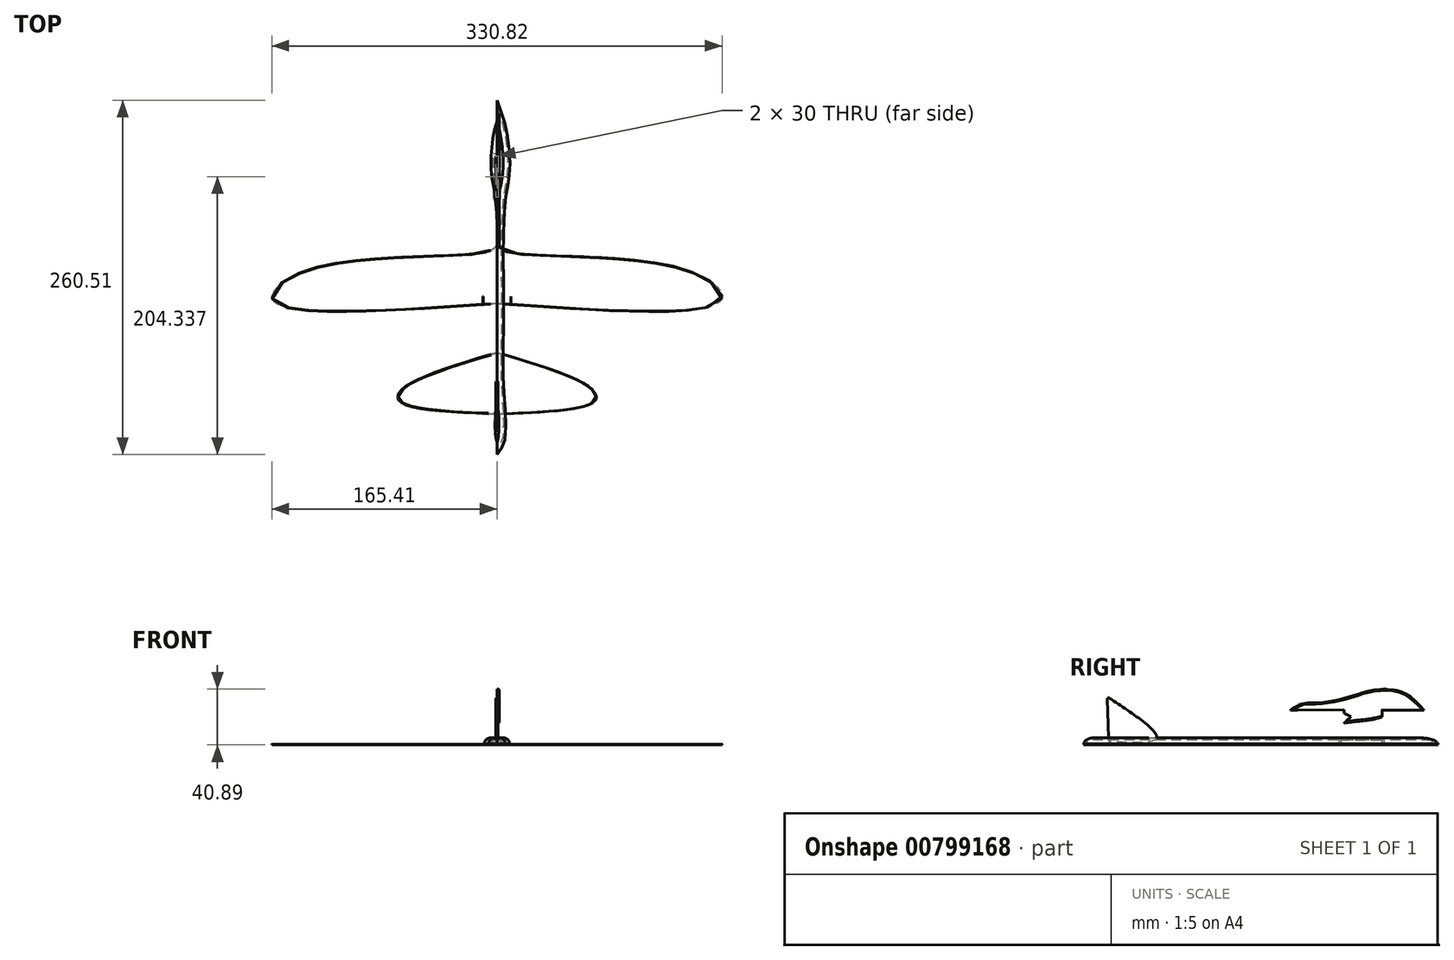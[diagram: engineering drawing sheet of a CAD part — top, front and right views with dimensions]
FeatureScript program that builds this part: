
annotation { "Feature Type Name" : "Feature", "Feature Type Description" : "" }
export const myFeature = defineFeature(function(context is Context, id is Id, definition is map)
    precondition{}
    {
        {
            var Q0;
            Q0=qCreatedBy(makeId("Top.planeOp"),FACE);
            var sketch = newSketch(context, id + "F0", { "sketchPlane" : qUnion([Q0])});
            skFitSpline(sketch, "E0", {"points": [v(0, 20.4) * mm, v(-6.56, 14.7) * mm, v(-134.74, 2.33) * mm, v(-164.69, -21.18) * mm, v(0, -23.65) * mm], "startDerivative": vector(-33.5, -72.01) * mm, "endDerivative": vector(609.3, 42.8) * mm});
            skFitSpline(sketch, "E1.MirrorCS", {"points": [v(0, 20.4) * mm, v(6.56, 14.7) * mm, v(134.74, 2.33) * mm, v(164.69, -21.18) * mm, v(0, -23.65) * mm], "startDerivative": vector(33.5, -72.01) * mm, "endDerivative": vector(-609.3, 42.8) * mm});
            skSolve(sketch);
        }
        {
            var Q0;
            Q0=makeQuery(id+"F0.imprint","IMPRINT",FACE,{"disambiguationData":[TD([[makeQuery(id+"F0.imprint","IMPRINT",EDGE,{"derivedFrom":sQuery(id+"F0.wireOp",EDGE,"E0")}),1.0]])]});
            extrude(context, id + "F1", {"entities" : qUnion([Q0]), "depth" : 0.5 * mm, "offsetDistance" : 25 * mm});
        }
        {
            var Q0;
            Q0=makeQuery(id+"F1.opExtrude","CAP_EDGE",EDGE,{"disambiguationData":[OSD([sQuery(id+"F0.wireOp",EDGE,"E1.MirrorCS")])],"isStart":false});
            var Q1;
            Q1=makeQuery(id+"F1.opExtrude","CAP_EDGE",EDGE,{"disambiguationData":[OSD([sQuery(id+"F0.wireOp",EDGE,"E0")])],"isStart":false});
            fillet(context, id + "F2", {"entities" : qUnion([Q0, Q1]), "radius" : 0.2 * mm, "tangentPropagation" : true, "allowEdgeOverflow" : false});
        }
        {
            var Q0;
            Q0=makeQuery(id+"F1.opExtrude","SWEPT_BODY",BODY,{"disambiguationData":[OSD([sQuery(id+"F0.wireOp",EDGE,"E0"),sQuery(id+"F0.wireOp",EDGE,"E1.MirrorCS")])]});
            transform(context, id + "F3", {"entities" : qUnion([Q0]), "transformType" : TransformType.TRANSLATION_3D, "dx" : 0 * mm, "dy" : 0 * mm, "dz" : 10 * mm, "makeCopy" : false});
        }
        {
            var Q0;
            Q0=qCreatedBy(makeId("Top.planeOp"),FACE);
            var sketch = newSketch(context, id + "F4", { "sketchPlane" : qUnion([Q0])});
            skFitSpline(sketch, "E2", {"points": [v(0, 125.84) * mm, v(-7.47, 100.86) * mm, v(-9.14, 71.54) * mm, v(-5.8, 49.89) * mm, v(-4.8, -37.06) * mm, v(-4.8, -83.04) * mm, v(-5.47, -124.68) * mm, v(0, -134.67) * mm], "startDerivative": vector(-69.22, -190.24) * mm, "endDerivative": vector(80.33, -93.5) * mm});
            skFitSpline(sketch, "E3.MirrorCS", {"points": [v(0, 125.84) * mm, v(7.47, 100.86) * mm, v(9.14, 71.54) * mm, v(5.8, 49.89) * mm, v(4.8, -37.06) * mm, v(4.8, -83.04) * mm, v(5.47, -124.68) * mm, v(0, -134.67) * mm], "startDerivative": vector(69.22, -190.24) * mm, "endDerivative": vector(-80.33, -93.5) * mm});
            skSolve(sketch);
        }
        {
            var Q0;
            Q0 = qSketchRegion(id + "F4", true);
            extrude(context, id + "F5", {"entities" : qUnion([Q0]), "depth" : 5 * mm, "offsetDistance" : 25 * mm});
        }
        {
            var Q0;
            Q0=makeQuery(id+"F5.opExtrude","SWEPT_BODY",BODY,{"disambiguationData":[OSD([sQuery(id+"F4.wireOp",EDGE,"E2"),sQuery(id+"F4.wireOp",EDGE,"E3.MirrorCS")])]});
            transform(context, id + "F6", {"entities" : qUnion([Q0]), "transformType" : TransformType.TRANSLATION_3D, "dx" : 0 * mm, "dy" : 0 * mm, "dz" : 10 * mm, "makeCopy" : false});
        }
        {
            var Q0;
            Q0=makeQuery(id+"F5.opExtrude","CAP_FACE",FACE,{"disambiguationData":[OSD([sQuery(id+"F4.wireOp",EDGE,"E2"),sQuery(id+"F4.wireOp",EDGE,"E3.MirrorCS")])],"isStart":false});
            var sketch = newSketch(context, id + "F7", { "sketchPlane" : qUnion([Q0])});
            skLineSegment(sketch, "E4.bottom", {"start": v(1, 54.67) * mm, "end": v(-1, 54.67) * mm});
            skLineSegment(sketch, "E4.top", {"start": v(1, 84.67) * mm, "end": v(-1, 84.67) * mm});
            skLineSegment(sketch, "E4.left", {"start": v(1, 54.67) * mm, "end": v(1, 84.67) * mm});
            skLineSegment(sketch, "E4.right", {"start": v(-1, 54.67) * mm, "end": v(-1, 84.67) * mm});
            skPoint(sketch, "E4.middle", {"position": v(0, 69.67) * mm});
            skSolve(sketch);
        }
        {
            var Q0;
            Q0=makeQuery(id+"F7.imprint","IMPRINT",FACE,{"disambiguationData":[TD([[makeQuery(id+"F7.imprint","IMPRINT",EDGE,{"derivedFrom":sQuery(id+"F7.wireOp",EDGE,"E4.bottom")}),-1.0]])]});
            extrude(context, id + "F8", {"entities" : qUnion([Q0]), "operationType" : NewBodyOperationType.REMOVE, "oppositeDirection" : true, "depth" : 8.7 * mm, "offsetDistance" : 25 * mm});
        }
        {
            var Q0;
            Q0=qCreatedBy(makeId("Right.planeOp"),FACE);
            var sketch = newSketch(context, id + "F9", { "sketchPlane" : qUnion([Q0])});
            skFitSpline(sketch, "E5", {"points": [v(-67.6, 50.99) * mm, v(-31.42, 20.75) * mm, v(-66.78, 18.05) * mm], "startDerivative": vector(106.02, -70.02) * mm, "endDerivative": vector(-109.5, 5.95) * mm});
            skLineSegment(sketch, "E6", {"start": v(-67.6, 50.99) * mm, "end": v(-66.78, 18.05) * mm});
            skSolve(sketch);
        }
        {
            var Q0;
            Q0 = qSketchRegion(id + "F9", true);
            extrude(context, id + "F10", {"entities" : qUnion([Q0]), "depth" : 1.6 * mm, "offsetDistance" : 25 * mm});
        }
        {
            var Q0;
            Q0=makeQuery(id+"F10.opExtrude","SWEPT_BODY",BODY,{"disambiguationData":[OSD([sQuery(id+"F9.wireOp",EDGE,"E5"),sQuery(id+"F9.wireOp",EDGE,"E6")])]});
            transform(context, id + "F11", {"entities" : qUnion([Q0]), "transformType" : TransformType.TRANSLATION_3D, "dx" : -0.8 * mm, "dy" : 0 * mm, "dz" : 0 * mm, "makeCopy" : false});
        }
        {
            var Q0;
            Q0=makeQuery(id+"F10.opExtrude","CAP_EDGE",EDGE,{"disambiguationData":[OSD([sQuery(id+"F9.wireOp",EDGE,"E6")])],"isStart":false});
            var Q1;
            Q1=makeQuery(id+"F10.opExtrude","SWEPT_FACE",FACE,{"disambiguationData":[OSD([sQuery(id+"F9.wireOp",EDGE,"E6")])]});
            var Q2;
            Q2=makeQuery(id+"F10.opExtrude","CAP_EDGE",EDGE,{"disambiguationData":[OSD([sQuery(id+"F9.wireOp",EDGE,"E5")])],"isStart":false});
            var Q3;
            Q3=makeQuery(id+"F10.opExtrude","CAP_EDGE",EDGE,{"disambiguationData":[OSD([sQuery(id+"F9.wireOp",EDGE,"E5")])],"isStart":true});
            fillet(context, id + "F12", {"entities" : qUnion([Q0, Q1, Q2, Q3]), "radius" : 0.8 * mm, "tangentPropagation" : true, "allowEdgeOverflow" : false});
        }
        {
            var Q0;
            Q0=makeQuery(id+"F10.opExtrude","SWEPT_BODY",BODY,{"disambiguationData":[OSD([sQuery(id+"F9.wireOp",EDGE,"E5"),sQuery(id+"F9.wireOp",EDGE,"E6")])]});
            transform(context, id + "F13", {"entities" : qUnion([Q0]), "transformType" : TransformType.TRANSLATION_3D, "dx" : 0 * mm, "dy" : -59.6 * mm, "dz" : -5.7 * mm, "makeCopy" : false});
        }
        {
            var Q0;
            Q0=qCreatedBy(makeId("Top.planeOp"),FACE);
            var sketch = newSketch(context, id + "F14", { "sketchPlane" : qUnion([Q0])});
            skFitSpline(sketch, "E7", {"points": [v(0, -59.7) * mm, v(70, -86.93) * mm, v(71.57, -95.53) * mm, v(0, -104.93) * mm], "startDerivative": vector(211.22, -63.23) * mm, "endDerivative": vector(-230.16, -8.83) * mm});
            skFitSpline(sketch, "E8.MirrorCS", {"points": [v(0, -59.7) * mm, v(-70, -86.93) * mm, v(-71.57, -95.53) * mm, v(0, -104.93) * mm], "startDerivative": vector(-211.22, -63.23) * mm, "endDerivative": vector(230.16, -8.83) * mm});
            skSolve(sketch);
        }
        {
            var Q0;
            Q0 = qSketchRegion(id + "F14", true);
            extrude(context, id + "F15", {"entities" : qUnion([Q0]), "depth" : 0.4 * mm, "offsetDistance" : 25 * mm});
        }
        {
            var Q0;
            Q0=makeQuery(id+"F15.opExtrude","CAP_EDGE",EDGE,{"disambiguationData":[OSD([sQuery(id+"F14.wireOp",EDGE,"E8.MirrorCS")])],"isStart":false});
            fillet(context, id + "F16", {"entities" : qUnion([Q0]), "radius" : 0.4 * mm, "tangentPropagation" : true, "allowEdgeOverflow" : false});
        }
        {
            var Q0;
            Q0=makeQuery(id+"F15.opExtrude","SWEPT_BODY",BODY,{"disambiguationData":[OSD([sQuery(id+"F14.wireOp",EDGE,"E7"),sQuery(id+"F14.wireOp",EDGE,"E8.MirrorCS")])]});
            transform(context, id + "F17", {"entities" : qUnion([Q0]), "transformType" : TransformType.TRANSLATION_3D, "dx" : 0 * mm, "dy" : 0 * mm, "dz" : 10 * mm, "makeCopy" : false});
        }
        {
            var Q0;
            Q0=qCreatedBy(makeId("Right.planeOp"),FACE);
            var sketch = newSketch(context, id + "F18", { "sketchPlane" : qUnion([Q0])});
            skPoint(sketch, "E9.startSnap0", {"position": v(57.57, 31.32) * mm});
            skLineSegment(sketch, "E10", {"start": v(84.75, 30.6) * mm, "end": v(84.75, 35.6) * mm});
            skLineSegment(sketch, "E11", {"start": v(84.75, 35.6) * mm, "end": v(115.57, 35.6) * mm});
            skFitSpline(sketch, "E12", {"points": [v(115.57, 35.6) * mm, v(99.54, 48.66) * mm, v(78.48, 50.2) * mm, v(61.24, 45.46) * mm, v(39.88, 41.04) * mm, v(25.84, 40.12) * mm, v(17.19, 35.6) * mm], "startDerivative": vector(-79.55, 85.9) * mm, "endDerivative": vector(-64.6, -44.24) * mm});
            skLineSegment(sketch, "E13", {"start": v(56.78, 33.1) * mm, "end": v(56.78, 35.73) * mm});
            skLineSegment(sketch, "E14", {"start": v(56.78, 35.73) * mm, "end": v(22.52, 35.6) * mm});
            skLineSegment(sketch, "E15", {"start": v(22.52, 35.6) * mm, "end": v(17.19, 35.6) * mm});
            skLineSegment(sketch, "E16", {"start": v(56.78, 33.1) * mm, "end": v(61.88, 30.63) * mm});
            skLineSegment(sketch, "E17", {"start": v(61.88, 30.63) * mm, "end": v(56.78, 26.05) * mm});
            skFitSpline(sketch, "E18", {"points": [v(84.75, 30.6) * mm, v(56.78, 26.05) * mm], "startDerivative": vector(-21.38, -9.06) * mm, "endDerivative": vector(-27.97, -4.55) * mm});
            skSolve(sketch);
        }
        {
            var Q0;
            Q0=makeQuery(id+"F10.opExtrude","SWEPT_BODY",BODY,{"disambiguationData":[OSD([sQuery(id+"F9.wireOp",EDGE,"E5"),sQuery(id+"F9.wireOp",EDGE,"E6")])]});
            transform(context, id + "F19", {"entities" : qUnion([Q0]), "transformType" : TransformType.TRANSLATION_3D, "dx" : 0 * mm, "dy" : 10 * mm, "dz" : 0 * mm, "makeCopy" : false});
        }
        {
            var Q0;
            Q0=makeQuery(id+"F18.imprint","IMPRINT",FACE,{"disambiguationData":[TD([[makeQuery(id+"F18.imprint","IMPRINT",EDGE,{"derivedFrom":sQuery(id+"F18.wireOp",EDGE,"E10")}),1.0]])]});
            extrude(context, id + "F20", {"entities" : qUnion([Q0]), "depth" : 1.7 * mm, "offsetDistance" : 25 * mm});
        }
        {
            var Q0;
            Q0=makeQuery(id+"F20.opExtrude","CAP_EDGE",EDGE,{"disambiguationData":[OSD([sQuery(id+"F18.wireOp",EDGE,"E12")])],"isStart":false});
            var Q1;
            Q1=makeQuery(id+"F20.opExtrude","CAP_EDGE",EDGE,{"disambiguationData":[OSD([sQuery(id+"F18.wireOp",EDGE,"E10")])],"isStart":false});
            var Q2;
            Q2=makeQuery(id+"F20.opExtrude","CAP_EDGE",EDGE,{"disambiguationData":[OSD([sQuery(id+"F18.wireOp",EDGE,"E18")])],"isStart":false});
            fillet(context, id + "F21", {"entities" : qUnion([Q0, Q1, Q2]), "radius" : 0.85 * mm, "tangentPropagation" : true, "allowEdgeOverflow" : false});
        }
        {
            var Q0;
            Q0=makeQuery(id+"F5.opExtrude","CAP_FACE",FACE,{"disambiguationData":[OSD([sQuery(id+"F4.wireOp",EDGE,"E2"),sQuery(id+"F4.wireOp",EDGE,"E3.MirrorCS")])],"isStart":true});
            shell(context, id + "F22", {"entities" : qUnion([Q0]), "thickness" : 1.6 * mm});
        }
        {
            var Q0;
            Q0=makeQuery(id+"F4.imprint","IMPRINT",FACE,{"disambiguationData":[TD([[makeQuery(id+"F4.imprint","IMPRINT",EDGE,{"derivedFrom":sQuery(id+"F4.wireOp",EDGE,"E2")}),1.0]])]});
            extrude(context, id + "F23", {"entities" : qUnion([Q0]), "depth" : 0.4 * mm, "offsetDistance" : 25 * mm});
        }
        {
            var Q0;
            Q0=makeQuery(id+"F23.opExtrude","SWEPT_BODY",BODY,{"disambiguationData":[OSD([sQuery(id+"F4.wireOp",EDGE,"E2"),sQuery(id+"F4.wireOp",EDGE,"E3.MirrorCS")])]});
            transform(context, id + "F24", {"entities" : qUnion([Q0]), "transformType" : TransformType.TRANSLATION_3D, "dx" : 0 * mm, "dy" : 0 * mm, "dz" : 0 * mm, "makeCopy" : false});
        }
        {
            var Q0;
            Q0=makeQuery(id+"F23.opExtrude","SWEPT_BODY",BODY,{"disambiguationData":[OSD([sQuery(id+"F4.wireOp",EDGE,"E2"),sQuery(id+"F4.wireOp",EDGE,"E3.MirrorCS")])]});
            transform(context, id + "F25", {"entities" : qUnion([Q0]), "transformType" : TransformType.TRANSLATION_3D, "dx" : 0 * mm, "dy" : 0 * mm, "dz" : 0 * mm, "makeCopy" : false});
        }
        {
            var Q0;
            Q0=makeQuery(id+"F0.imprint","IMPRINT",FACE,{"disambiguationData":[TD([[makeQuery(id+"F0.imprint","IMPRINT",EDGE,{"derivedFrom":sQuery(id+"F0.wireOp",EDGE,"E0")}),1.0]])]});
            var sketch = newSketch(context, id + "F26", { "sketchPlane" : qUnion([Q0])});
            skLineSegment(sketch, "E19.bottom", {"start": v(-10.12, -18.5) * mm, "end": v(-10.32, -18.5) * mm});
            skLineSegment(sketch, "E19.top", {"start": v(-10.12, -24.5) * mm, "end": v(-10.32, -24.5) * mm});
            skLineSegment(sketch, "E19.left", {"start": v(-10.12, -18.5) * mm, "end": v(-10.12, -24.5) * mm});
            skLineSegment(sketch, "E19.right", {"start": v(-10.32, -18.5) * mm, "end": v(-10.32, -24.5) * mm});
            skLineSegment(sketch, "E20.MirrorCS", {"start": v(10.32, -18.5) * mm, "end": v(10.32, -24.5) * mm});
            skLineSegment(sketch, "E21.MirrorCS", {"start": v(10.12, -18.5) * mm, "end": v(10.12, -24.5) * mm});
            skLineSegment(sketch, "E22.MirrorCS", {"start": v(10.12, -18.5) * mm, "end": v(10.32, -18.5) * mm});
            skLineSegment(sketch, "E23.MirrorCS", {"start": v(10.12, -24.5) * mm, "end": v(10.32, -24.5) * mm});
            skSolve(sketch);
        }
        {
            var Q0;
            Q0 = qSketchRegion(id + "F26", true);
            extrude(context, id + "F27", {"entities" : qUnion([Q0]), "operationType" : NewBodyOperationType.REMOVE, "depth" : 42.7 * mm, "offsetDistance" : 25 * mm});
        }
        {
            var Q0;
            Q0=makeQuery(id+"F15.opExtrude","CAP_EDGE",EDGE,{"disambiguationData":[OSD([sQuery(id+"F14.wireOp",EDGE,"E8.MirrorCS")])],"isStart":true});
            var Q1;
            Q1=makeQuery(id+"F15.opExtrude","CAP_EDGE",EDGE,{"disambiguationData":[OSD([sQuery(id+"F14.wireOp",EDGE,"E7")])],"isStart":true});
            fillet(context, id + "F28", {"entities" : qUnion([Q0, Q1]), "radius" : 0.2 * mm, "tangentPropagation" : true, "allowEdgeOverflow" : false});
        }
        {
            var Q0;
            Q0=makeQuery(id+"F23.opExtrude","SWEPT_BODY",BODY,{"disambiguationData":[OSD([sQuery(id+"F4.wireOp",EDGE,"E2"),sQuery(id+"F4.wireOp",EDGE,"E3.MirrorCS")])]});
            transform(context, id + "F29", {"entities" : qUnion([Q0]), "transformType" : TransformType.TRANSLATION_3D, "dx" : 0 * mm, "dy" : 0 * mm, "dz" : 10.2 * mm, "makeCopy" : false});
        }
        {
            var Q0;
            Q0=makeQuery(id+"F5.opExtrude","SWEPT_BODY",BODY,{"disambiguationData":[OSD([sQuery(id+"F4.wireOp",EDGE,"E2"),sQuery(id+"F4.wireOp",EDGE,"E3.MirrorCS")])]});
            transform(context, id + "F30", {"entities" : qUnion([Q0]), "transformType" : TransformType.TRANSLATION_3D, "dx" : 0 * mm, "dy" : 0 * mm, "dz" : 5 * mm, "makeCopy" : false});
        }
        {
            var Q0;
            Q0=makeQuery(id+"F5.opExtrude","SWEPT_BODY",BODY,{"disambiguationData":[OSD([sQuery(id+"F4.wireOp",EDGE,"E2"),sQuery(id+"F4.wireOp",EDGE,"E3.MirrorCS")])]});
            transform(context, id + "F31", {"entities" : qUnion([Q0]), "transformType" : TransformType.TRANSLATION_3D, "dx" : 0 * mm, "dy" : 0 * mm, "dz" : -5 * mm, "makeCopy" : false});
        }
        {
            var Q0;
            Q0=makeQuery(id+"F5.opExtrude","CAP_EDGE",EDGE,{"disambiguationData":[OSD([sQuery(id+"F4.wireOp",EDGE,"E3.MirrorCS")])],"isStart":false});
            var Q1;
            Q1=makeQuery(id+"F5.opExtrude","CAP_EDGE",EDGE,{"disambiguationData":[OSD([sQuery(id+"F4.wireOp",EDGE,"E2")])],"isStart":false});
            fillet(context, id + "F32", {"entities" : qUnion([Q0, Q1]), "radius" : 5 * mm, "tangentPropagation" : true, "allowEdgeOverflow" : false});
        }
        {
            var Q0;
            Q0=makeQuery(id+"F23.opExtrude","SWEPT_BODY",BODY,{"disambiguationData":[OSD([sQuery(id+"F4.wireOp",EDGE,"E2"),sQuery(id+"F4.wireOp",EDGE,"E3.MirrorCS")])]});
            var Q1;
            Q1=makeQuery(id+"F5.opExtrude","SWEPT_BODY",BODY,{"disambiguationData":[OSD([sQuery(id+"F4.wireOp",EDGE,"E2"),sQuery(id+"F4.wireOp",EDGE,"E3.MirrorCS")])]});
            transform(context, id + "F33", {"entities" : qUnion([Q0, Q1]), "transformType" : TransformType.TRANSLATION_3D, "dx" : 0 * mm, "dy" : 0 * mm, "dz" : 0.2 * mm, "makeCopy" : false});
        }
    });
